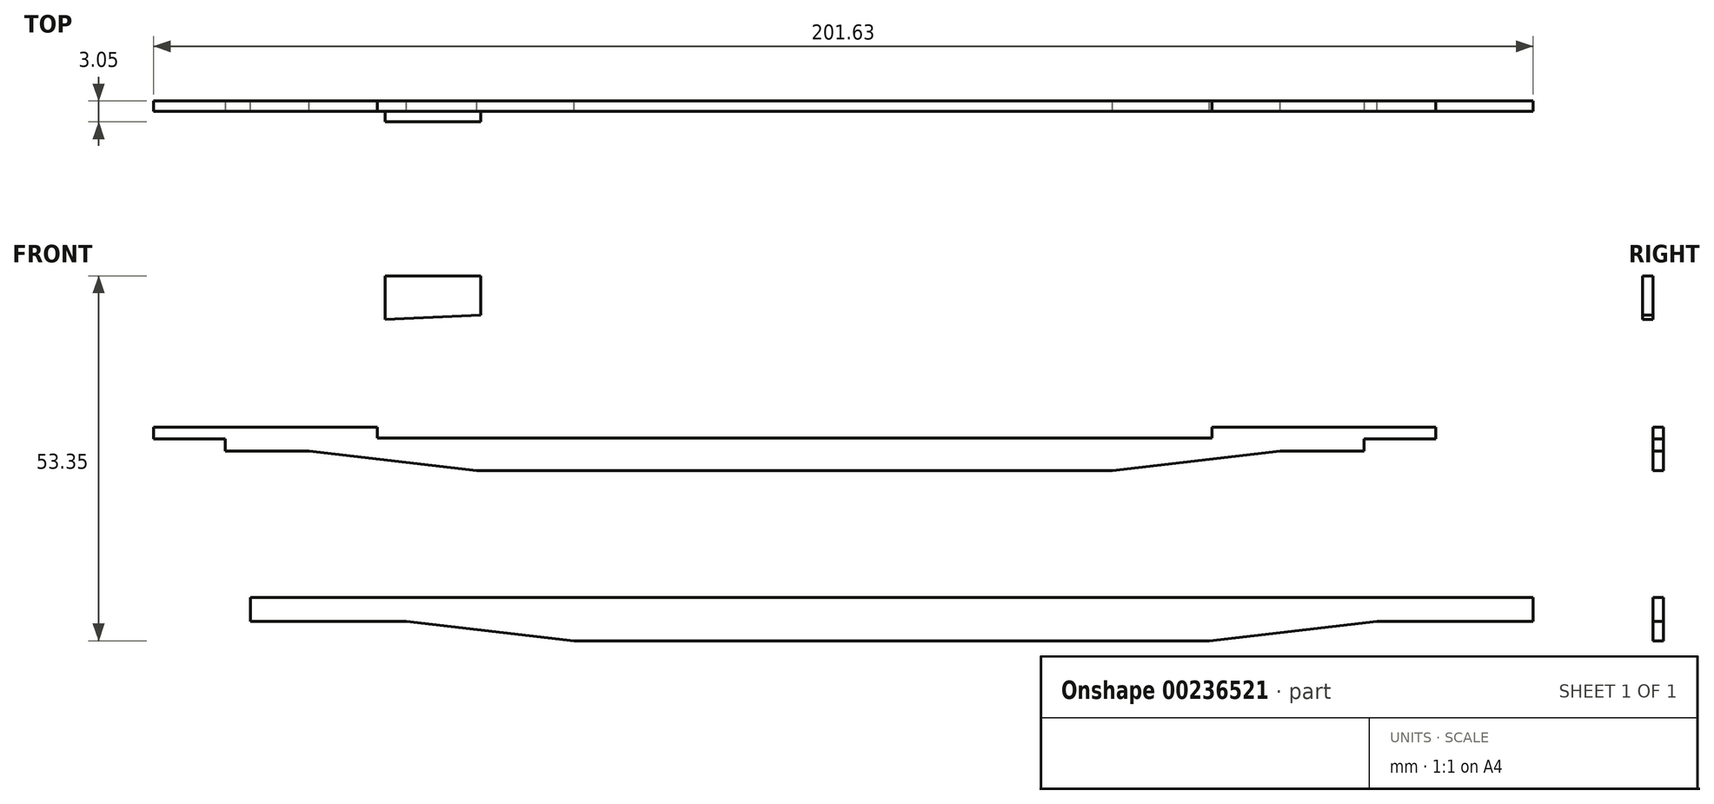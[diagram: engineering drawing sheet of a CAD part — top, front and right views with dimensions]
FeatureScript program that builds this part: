
annotation { "Feature Type Name" : "Feature", "Feature Type Description" : "" }
export const myFeature = defineFeature(function(context is Context, id is Id, definition is map)
    precondition{}
    {
        {
            var Q0;
            Q0=qCreatedBy(makeId("Front.planeOp"),FACE);
            var sketch = newSketch(context, id + "F0", { "sketchPlane" : qUnion([Q0])});
            skLineSegment(sketch, "E0", {"start": v(-62.37, 15.12) * mm, "end": v(125.06, 15.12) * mm});
            skLineSegment(sketch, "E1", {"start": v(125.06, 15.12) * mm, "end": v(125.06, 11.62) * mm});
            skLineSegment(sketch, "E2", {"start": v(125.06, 11.62) * mm, "end": v(102.3, 11.62) * mm});
            skLineSegment(sketch, "E3", {"start": v(102.3, 11.62) * mm, "end": v(77.77, 8.77) * mm});
            skLineSegment(sketch, "E4", {"start": v(77.77, 8.77) * mm, "end": v(-15.08, 8.77) * mm});
            skLineSegment(sketch, "E5", {"start": v(-15.08, 8.77) * mm, "end": v(-39.6, 11.62) * mm});
            skLineSegment(sketch, "E6", {"start": v(-39.6, 11.62) * mm, "end": v(-62.37, 11.62) * mm});
            skLineSegment(sketch, "E7", {"start": v(-62.37, 11.62) * mm, "end": v(-62.37, 15.12) * mm});
            skSolve(sketch);
        }
        {
            var Q0;
            Q0=makeQuery(id+"F0.imprint","IMPRINT",FACE,{"disambiguationData":[TD([[makeQuery(id+"F0.imprint","IMPRINT",EDGE,{"derivedFrom":sQuery(id+"F0.wireOp",EDGE,"E0")}),-1.0]])]});
            extrude(context, id + "F1", {"entities" : qUnion([Q0]), "depth" : 1.52 * mm});
        }
        {
            var Q0;
            Q0=makeQuery(id+"F1.opExtrude","SWEPT_BODY",BODY,{"disambiguationData":[OSD([sQuery(id+"F0.wireOp",EDGE,"E0"),sQuery(id+"F0.wireOp",EDGE,"E1"),sQuery(id+"F0.wireOp",EDGE,"E2"),sQuery(id+"F0.wireOp",EDGE,"E3"),sQuery(id+"F0.wireOp",EDGE,"E4"),sQuery(id+"F0.wireOp",EDGE,"E5"),sQuery(id+"F0.wireOp",EDGE,"E6"),sQuery(id+"F0.wireOp",EDGE,"E7")])]});
            transform(context, id + "F2", {"entities" : qUnion([Q0]), "transformType" : TransformType.TRANSLATION_3D, "dx" : -14.2 * mm, "dy" : 0 * mm, "dz" : 24.9 * mm, "makeCopy" : true});
        }
        {
            var Q0;
            Q0=makeQuery(id+"F2.opPattern","COPY",FACE,{"derivedFrom":makeQuery(id+"F1.opExtrude","CAP_FACE",FACE,{"disambiguationData":[OSD([sQuery(id+"F0.wireOp",EDGE,"E0"),sQuery(id+"F0.wireOp",EDGE,"E1"),sQuery(id+"F0.wireOp",EDGE,"E2"),sQuery(id+"F0.wireOp",EDGE,"E3"),sQuery(id+"F0.wireOp",EDGE,"E4"),sQuery(id+"F0.wireOp",EDGE,"E5"),sQuery(id+"F0.wireOp",EDGE,"E6"),sQuery(id+"F0.wireOp",EDGE,"E7")])],"isStart":false}),"instanceName":"1"});
            var sketch = newSketch(context, id + "F3", { "sketchPlane" : qUnion([Q0])});
            skLineSegment(sketch, "E8", {"start": v(-76.57, 38.27) * mm, "end": v(-66.06, 38.27) * mm});
            skLineSegment(sketch, "E9", {"start": v(-66.06, 38.27) * mm, "end": v(-66.06, 36.52) * mm});
            skSolve(sketch);
        }
        {
            var Q0;
            {var subQ0=sQuery(id+"F3.wireOp",EDGE,"E8");Q0=makeQuery(id+"F3.imprint","IMPRINT",FACE,{"disambiguationData":[TD([[makeQuery(id+"F3.imprint","IMPRINT",EDGE,{"derivedFrom":subQ0}),-1.0]])]});}
            extrude(context, id + "F4", {"entities" : qUnion([Q0]), "operationType" : NewBodyOperationType.REMOVE, "oppositeDirection" : true, "depth" : 1.52 * mm});
        }
        {
            var Q0;
            Q0=makeQuery(id+"F2.opPattern","COPY",FACE,{"derivedFrom":makeQuery(id+"F1.opExtrude","CAP_FACE",FACE,{"disambiguationData":[OSD([sQuery(id+"F0.wireOp",EDGE,"E0"),sQuery(id+"F0.wireOp",EDGE,"E1"),sQuery(id+"F0.wireOp",EDGE,"E2"),sQuery(id+"F0.wireOp",EDGE,"E3"),sQuery(id+"F0.wireOp",EDGE,"E4"),sQuery(id+"F0.wireOp",EDGE,"E5"),sQuery(id+"F0.wireOp",EDGE,"E6"),sQuery(id+"F0.wireOp",EDGE,"E7")])],"isStart":false}),"instanceName":"1"});
            var sketch = newSketch(context, id + "F5", { "sketchPlane" : qUnion([Q0])});
            skLineSegment(sketch, "E10", {"start": v(110.86, 38.27) * mm, "end": v(100.35, 38.27) * mm});
            skLineSegment(sketch, "E11", {"start": v(100.35, 38.27) * mm, "end": v(100.35, 36.52) * mm});
            skSolve(sketch);
        }
        {
            var Q0;
            {var subQ0=sQuery(id+"F5.wireOp",EDGE,"E10");Q0=makeQuery(id+"F5.imprint","IMPRINT",FACE,{"disambiguationData":[TD([[makeQuery(id+"F5.imprint","IMPRINT",EDGE,{"derivedFrom":subQ0}),1.0]])]});}
            extrude(context, id + "F6", {"entities" : qUnion([Q0]), "operationType" : NewBodyOperationType.REMOVE, "oppositeDirection" : true, "depth" : 1.52 * mm});
        }
        {
            var Q0;
            Q0=makeQuery(id+"F2.opPattern","COPY",FACE,{"derivedFrom":makeQuery(id+"F1.opExtrude","SWEPT_FACE",FACE,{"disambiguationData":[OSD([sQuery(id+"F0.wireOp",EDGE,"E0")])]}),"instanceName":"1"});
            var sketch = newSketch(context, id + "F7", { "sketchPlane" : qUnion([Q0])});
            skLineSegment(sketch, "E12", {"start": v(-43.85, -1.52) * mm, "end": v(78.15, -1.52) * mm});
            skLineSegment(sketch, "E13", {"start": v(78.15, -1.52) * mm, "end": v(78.15, 0) * mm});
            skLineSegment(sketch, "E14", {"start": v(78.15, 0) * mm, "end": v(-43.85, 0) * mm});
            skLineSegment(sketch, "E15", {"start": v(-43.85, 0) * mm, "end": v(-43.85, -1.52) * mm});
            skSolve(sketch);
        }
        {
            var Q0;
            Q0 = qSketchRegion(id + "F7", true);
            extrude(context, id + "F8", {"entities" : qUnion([Q0]), "operationType" : NewBodyOperationType.REMOVE, "oppositeDirection" : true, "depth" : 1.6 * mm, "offsetDistance" : 25 * mm});
        }
        {
            var Q0;
            Q0=makeQuery(id+"F2.opPattern","COPY",FACE,{"derivedFrom":makeQuery(id+"F1.opExtrude","CAP_FACE",FACE,{"disambiguationData":[OSD([sQuery(id+"F0.wireOp",EDGE,"E0"),sQuery(id+"F0.wireOp",EDGE,"E1"),sQuery(id+"F0.wireOp",EDGE,"E2"),sQuery(id+"F0.wireOp",EDGE,"E3"),sQuery(id+"F0.wireOp",EDGE,"E4"),sQuery(id+"F0.wireOp",EDGE,"E5"),sQuery(id+"F0.wireOp",EDGE,"E6"),sQuery(id+"F0.wireOp",EDGE,"E7")])],"isStart":false}),"instanceName":"1"});
            var sketch = newSketch(context, id + "F9", { "sketchPlane" : qUnion([Q0])});
            skLineSegment(sketch, "E16", {"start": v(-42.71, 62.12) * mm, "end": v(-28.7, 62.12) * mm});
            skLineSegment(sketch, "E17", {"start": v(-42.71, 62.12) * mm, "end": v(-42.71, 55.77) * mm});
            skLineSegment(sketch, "E18", {"start": v(-28.7, 62.12) * mm, "end": v(-28.7, 56.35) * mm});
            skLineSegment(sketch, "E19", {"start": v(-42.71, 55.77) * mm, "end": v(-28.7, 56.35) * mm});
            skSolve(sketch);
        }
        {
            var Q0;
            Q0=makeQuery(id+"F9.imprint","IMPRINT",FACE,{"disambiguationData":[TD([[makeQuery(id+"F9.imprint","IMPRINT",EDGE,{"derivedFrom":sQuery(id+"F9.wireOp",EDGE,"E16")}),-1.0]])]});
            extrude(context, id + "F10", {"entities" : qUnion([Q0]), "depth" : 1.52 * mm, "offsetDistance" : 25 * mm});
        }
    });
